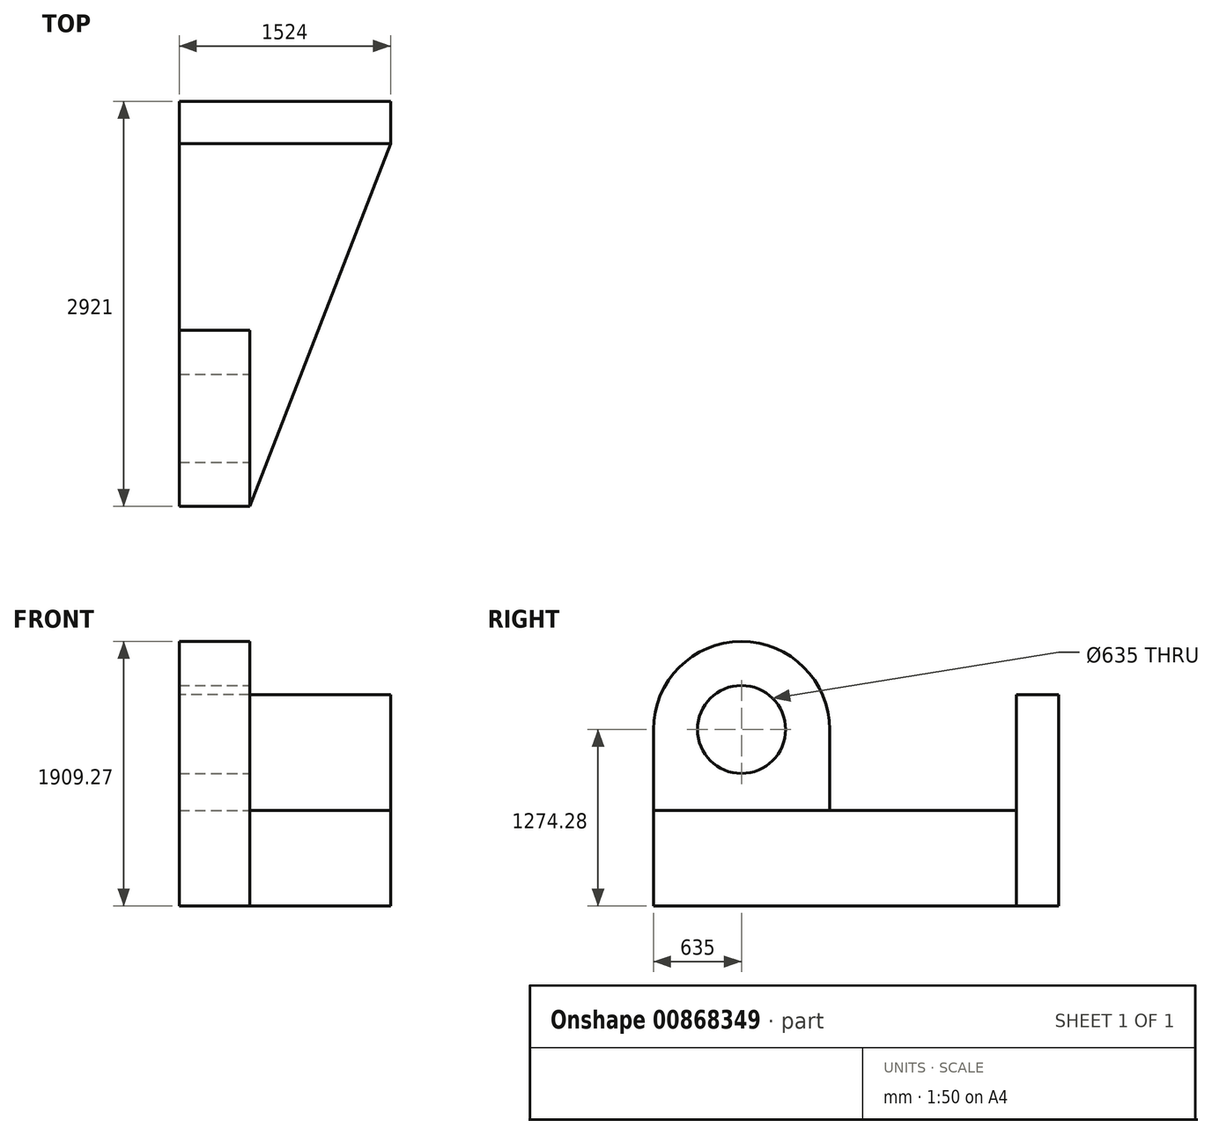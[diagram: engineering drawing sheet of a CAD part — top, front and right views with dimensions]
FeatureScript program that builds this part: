
annotation { "Feature Type Name" : "Feature", "Feature Type Description" : "" }
export const myFeature = defineFeature(function(context is Context, id is Id, definition is map)
    precondition{}
    {
        {
            var Q0;
            Q0=qCreatedBy(makeId("Front.planeOp"),FACE);
            var sketch = newSketch(context, id + "F0", { "sketchPlane" : qUnion([Q0])});
            skLineSegment(sketch, "E0.bottom", {"start": v(0, 0) * mm, "end": v(-1524, 0) * mm});
            skLineSegment(sketch, "E0.top", {"start": v(0, 1524) * mm, "end": v(-1524, 1524) * mm});
            skLineSegment(sketch, "E0.left", {"start": v(0, 0) * mm, "end": v(0, 1524) * mm});
            skLineSegment(sketch, "E0.right", {"start": v(-1524, 0) * mm, "end": v(-1524, 1524) * mm});
            skSolve(sketch);
        }
        {
            var Q0;
            Q0=makeQuery(id+"F0.imprint","IMPRINT",FACE,{"disambiguationData":[TD([[makeQuery(id+"F0.imprint","IMPRINT",EDGE,{"derivedFrom":sQuery(id+"F0.wireOp",EDGE,"E0.bottom")}),-1.0]])]});
            extrude(context, id + "F1", {"entities" : qUnion([Q0]), "depth" : 304.8 * mm, "offsetDistance" : 25.4 * mm});
        }
        {
            var Q0;
            Q0=makeQuery(id+"F1.opExtrude","CAP_FACE",FACE,{"disambiguationData":[OSD([sQuery(id+"F0.wireOp",EDGE,"E0.bottom"),sQuery(id+"F0.wireOp",EDGE,"E0.top"),sQuery(id+"F0.wireOp",EDGE,"E0.left"),sQuery(id+"F0.wireOp",EDGE,"E0.right")])],"isStart":false});
            var sketch = newSketch(context, id + "F2", { "sketchPlane" : qUnion([Q0])});
            skLineSegment(sketch, "E1.bottom", {"start": v(-1524, 0) * mm, "end": v(0, 0) * mm});
            skLineSegment(sketch, "E1.top", {"start": v(-1524, 690.07) * mm, "end": v(0, 690.07) * mm});
            skLineSegment(sketch, "E1.left", {"start": v(-1524, 0) * mm, "end": v(-1524, 690.07) * mm});
            skLineSegment(sketch, "E1.right", {"start": v(0, 0) * mm, "end": v(0, 690.07) * mm});
            skSolve(sketch);
        }
        {
            var Q0;
            Q0=makeQuery(id+"F2.imprint","IMPRINT",FACE,{"disambiguationData":[TD([[makeQuery(id+"F2.imprint","IMPRINT",EDGE,{"derivedFrom":sQuery(id+"F2.wireOp",EDGE,"E1.bottom")}),-1.0]])]});
            extrude(context, id + "F3", {"entities" : qUnion([Q0]), "operationType" : NewBodyOperationType.ADD, "depth" : 2616.2 * mm, "offsetDistance" : 25.4 * mm});
        }
        {
            var Q0;
            Q0=makeQuery(id+"F3.opExtrude","SWEPT_FACE",FACE,{"disambiguationData":[OSD([sQuery(id+"F2.wireOp",EDGE,"E1.top")])]});
            var sketch = newSketch(context, id + "F4", { "sketchPlane" : qUnion([Q0])});
            skLineSegment(sketch, "E2.bottom", {"start": v(-1524, -2921) * mm, "end": v(-1016, -2921) * mm});
            skLineSegment(sketch, "E2.top", {"start": v(-1524, -1651) * mm, "end": v(-1016, -1651) * mm});
            skLineSegment(sketch, "E2.left", {"start": v(-1524, -2921) * mm, "end": v(-1524, -1651) * mm});
            skLineSegment(sketch, "E2.right", {"start": v(-1016, -2921) * mm, "end": v(-1016, -1651) * mm});
            skSolve(sketch);
        }
        {
            var Q0;
            Q0=makeQuery(id+"F4.imprint","IMPRINT",FACE,{"disambiguationData":[TD([[makeQuery(id+"F4.imprint","IMPRINT",EDGE,{"derivedFrom":sQuery(id+"F4.wireOp",EDGE,"E2.bottom")}),1.0]])]});
            extrude(context, id + "F5", {"entities" : qUnion([Q0]), "operationType" : NewBodyOperationType.ADD, "depth" : 584.2 * mm, "offsetDistance" : 25.4 * mm});
        }
        {
            var Q0;
            Q0=makeQuery(id+"F5.opExtrude","SWEPT_FACE",FACE,{"disambiguationData":[OSD([sQuery(id+"F4.wireOp",EDGE,"E2.right")])]});
            var sketch = newSketch(context, id + "F6", { "sketchPlane" : qUnion([Q0])});
            skCircle(sketch, "E3", {"center": v(-2286, 1274.27) * mm, "radius": 635 * mm});
            skSolve(sketch);
        }
        {
            var Q0;
            {var subQ1=sQuery(id+"F4.wireOp",EDGE,"E2.right");var subQ2=makeQuery(id+"F5.opExtrude","CAP_EDGE",EDGE,{"disambiguationData":[OSD([subQ1])],"isStart":false});Q0=makeQuery(id+"F6.imprint","IMPRINT",FACE,{"disambiguationData":[TD([[makeQuery(id+"F6.imprint","IMPRINT",EDGE,{"derivedFrom":subQ2}),1.0]])]});}
            extrude(context, id + "F7", {"entities" : qUnion([Q0]), "operationType" : NewBodyOperationType.ADD, "oppositeDirection" : true, "depth" : 508 * mm, "offsetDistance" : 25.4 * mm});
        }
        {
            var Q0;
            Q0=makeQuery(id+"F1cKuRCtTCnWeOU_1.imprint","IMPRINT",FACE,{"disambiguationData":[TD([[makeQuery(id+"F1cKuRCtTCnWeOU_1.imprint","IMPRINT",EDGE,{"derivedFrom":sQuery(id+"F1cKuRCtTCnWeOU_1.wireOp",EDGE,"dWaPrdwJ-Bli8-s2KR-QQZX-kUUwZtn7z9yL")}),1.0]])]});
            var sketch = newSketch(context, id + "F8", { "sketchPlane" : qUnion([Q0])});
            skSolve(sketch);
        }
        {
            var Q0;
            Q0=makeQuery(id+"F3.opExtrude","SWEPT_FACE",FACE,{"disambiguationData":[OSD([sQuery(id+"F2.wireOp",EDGE,"E1.top")])]});
            var sketch = newSketch(context, id + "F9", { "sketchPlane" : qUnion([Q0])});
            skLineSegment(sketch, "E4", {"start": v(-1016, -2921) * mm, "end": v(0, -304.8) * mm});
            skLineSegment(sketch, "E5", {"start": v(0, -304.8) * mm, "end": v(0, -2921) * mm});
            skLineSegment(sketch, "E6", {"start": v(0, -2921) * mm, "end": v(-1016, -2921) * mm});
            skSolve(sketch);
        }
        {
            var Q0;
            {var subQ0=sQuery(id+"F4.wireOp",EDGE,"E2.right");Q0=makeQuery(id+"F7.boolean.opBoolean","MERGE",FACE,{"derivedFrom":[makeQuery(id+"F5.opExtrude","SWEPT_FACE",FACE,{"disambiguationData":[OSD([subQ0])]}),makeQuery(id+"F7.opExtrude","CAP_FACE",FACE,{"disambiguationData":[OSD([subQ0,sQuery(id+"F6.wireOp",EDGE,"E3")])],"isStart":true})]});}
            var sketch = newSketch(context, id + "F10", { "sketchPlane" : qUnion([Q0])});
            skCircle(sketch, "E7", {"center": v(-2286, 1274.27) * mm, "radius": 317.5 * mm});
            skSolve(sketch);
        }
        {
            var Q0;
            Q0=makeQuery(id+"F10.imprint","IMPRINT",FACE,{"disambiguationData":[TD([[makeQuery(id+"F10.imprint","IMPRINT",EDGE,{"derivedFrom":sQuery(id+"F10.wireOp",EDGE,"E7")}),1.0]])]});
            extrude(context, id + "F11", {"entities" : qUnion([Q0]), "operationType" : NewBodyOperationType.REMOVE, "oppositeDirection" : true, "depth" : 812.8 * mm, "offsetDistance" : 25.4 * mm});
        }
        {
            var Q0;
            Q0=makeQuery(id+"F9.imprint","IMPRINT",FACE,{"disambiguationData":[TD([[makeQuery(id+"F9.imprint","IMPRINT",EDGE,{"derivedFrom":sQuery(id+"F9.wireOp",EDGE,"E4")}),-1.0]])]});
            extrude(context, id + "F12", {"entities" : qUnion([Q0]), "operationType" : NewBodyOperationType.REMOVE, "oppositeDirection" : true, "depth" : 1864.36 * mm, "offsetDistance" : 25.4 * mm});
        }
    });
